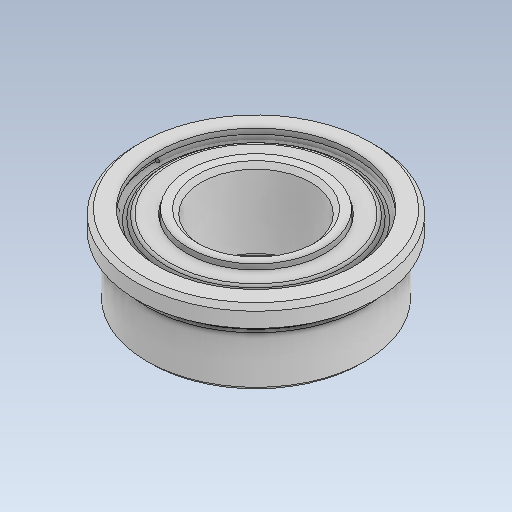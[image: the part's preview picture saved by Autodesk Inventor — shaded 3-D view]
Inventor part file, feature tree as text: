
AUTODESK INVENTOR PART (.ipt)
format: ipt  version: 2020 (Build 240168000, 168)  size: 270,336 bytes
history: native  units: in
note: dims shown in document units (in); Inventor stores cm internally (conversion verified against a paired STEP export)
features: revolve x1, fillet x1, mirror x1
ambient origin geometry x8: Origin, YZ Plane, XZ Plane, XY Plane, X Axis, Y Axis, Z Axis, Center Point
bodies: Solid1 (feature_tree), Solid2 (feature_tree), Solid3 (feature_tree)
feature tree (3):
  revolve  "Revolve1"  [1 undecoded]
  fillet  "Fillet1"  [1 undecoded]
  mirror  "Mirror8"
note: 2 required parameter values undecoded (feature->parameter linkage not recoverable at this tier; creation-order binding heuristic only, values carry confidence <= 0.55)
